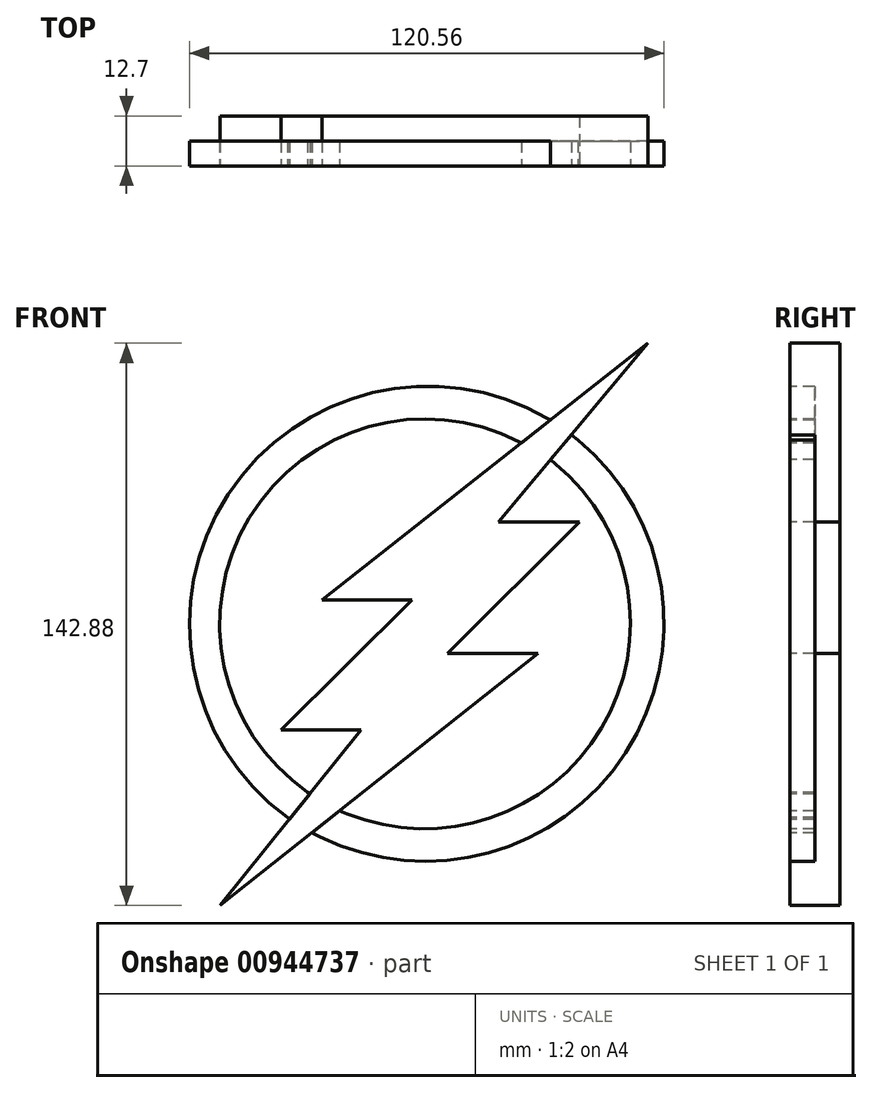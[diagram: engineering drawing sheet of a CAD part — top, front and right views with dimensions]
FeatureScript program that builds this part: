
annotation { "Feature Type Name" : "Feature", "Feature Type Description" : "" }
export const myFeature = defineFeature(function(context is Context, id is Id, definition is map)
    precondition{}
    {
        {
            var Q0;
            Q0=qCreatedBy(makeId("Front.planeOp"),FACE);
            var sketch = newSketch(context, id + "F0", { "sketchPlane" : qUnion([Q0])});
            skArc(sketch, "E0", {"start": v(8.9, 48.86) * mm, "mid": v(-59.71, 29.53) * mm, "end": v(-44.86, -40.17) * mm});
            skArc(sketch, "E1", {"start": v(-34.81, -45.6) * mm, "mid": v(29.76, -23.84) * mm, "end": v(18.12, 43.3) * mm});
            skArc(sketch, "E2", {"start": v(-41.74, -51.44) * mm, "mid": v(35.87, -30.16) * mm, "end": v(23.82, 49.4) * mm});
            skArc(sketch, "E3", {"start": v(16.08, 54.83) * mm, "mid": v(-65.07, 35.5) * mm, "end": v(-50.01, -46.55) * mm});
            skLineSegment(sketch, "E4", {"start": v(41.6, 73.97) * mm, "end": v(3.6, 28.5) * mm});
            skLineSegment(sketch, "E5", {"start": v(3.6, 28.5) * mm, "end": v(24.23, 28.5) * mm});
            skLineSegment(sketch, "E6", {"start": v(24.23, 28.5) * mm, "end": v(-9.3, -4.89) * mm});
            skLineSegment(sketch, "E7", {"start": v(-9.3, -4.89) * mm, "end": v(13.64, -4.89) * mm});
            skLineSegment(sketch, "E8", {"start": v(13.64, -4.89) * mm, "end": v(-65.08, -67.32) * mm});
            skLineSegment(sketch, "E9", {"start": v(-65.08, -67.32) * mm, "end": v(-67.09, -68.91) * mm});
            skLineSegment(sketch, "E10", {"start": v(-67.09, -68.91) * mm, "end": v(-31.27, -24.32) * mm});
            skLineSegment(sketch, "E11", {"start": v(-31.27, -24.32) * mm, "end": v(-51.63, -24.32) * mm});
            skLineSegment(sketch, "E12", {"start": v(-51.63, -24.32) * mm, "end": v(-18.38, 8.66) * mm});
            skLineSegment(sketch, "E13", {"start": v(-18.38, 8.66) * mm, "end": v(-41.18, 8.66) * mm});
            skLineSegment(sketch, "E14", {"start": v(-41.18, 8.66) * mm, "end": v(41.6, 73.97) * mm});
            skLineSegment(sketch, "E15", {"start": v(23.82, 49.4) * mm, "end": v(22.1, 50.64) * mm});
            skLineSegment(sketch, "E16", {"start": v(16.08, 54.83) * mm, "end": v(16.81, 54.41) * mm});
            skLineSegment(sketch, "E17", {"start": v(-50.01, -46.55) * mm, "end": v(-49.52, -47.05) * mm});
            skLineSegment(sketch, "E18", {"start": v(-41.74, -51.44) * mm, "end": v(-43.78, -50.43) * mm});
            skLineSegment(sketch, "E19", {"start": v(-41.18, 8.66) * mm, "end": v(-14.18, 19.27) * mm});
            skLineSegment(sketch, "E20", {"start": v(-14.18, 19.27) * mm, "end": v(3.6, 28.5) * mm});
            skLineSegment(sketch, "E21", {"start": v(-14.18, 19.27) * mm, "end": v(41.6, 73.97) * mm});
            skLineSegment(sketch, "E22", {"start": v(-14.18, 19.27) * mm, "end": v(2.38, 19.27) * mm});
            skLineSegment(sketch, "E23", {"start": v(2.38, 19.27) * mm, "end": v(24.23, 28.5) * mm});
            skLineSegment(sketch, "E24", {"start": v(2.38, 19.27) * mm, "end": v(-29.25, -14.25) * mm});
            skLineSegment(sketch, "E25", {"start": v(-29.25, -14.25) * mm, "end": v(-51.63, -24.32) * mm});
            skLineSegment(sketch, "E26", {"start": v(-29.25, -14.25) * mm, "end": v(-13.1, -14.25) * mm});
            skLineSegment(sketch, "E27", {"start": v(-13.1, -14.25) * mm, "end": v(13.64, -4.89) * mm});
            skLineSegment(sketch, "E28", {"start": v(-13.1, -14.25) * mm, "end": v(-67.09, -68.91) * mm});
            skLineSegment(sketch, "E29", {"start": v(-18.38, 8.66) * mm, "end": v(2.38, 19.27) * mm});
            skLineSegment(sketch, "E30", {"start": v(-31.27, -24.32) * mm, "end": v(-13.1, -14.25) * mm});
            skLineSegment(sketch, "E31", {"start": v(-29.25, -14.25) * mm, "end": v(-9.3, -4.89) * mm});
            skLineSegment(sketch, "E32", {"start": v(-34.81, -45.6) * mm, "end": v(-36.73, -44.83) * mm});
            skLineSegment(sketch, "E33", {"start": v(-44.27, -40.5) * mm, "end": v(-44.86, -40.17) * mm});
            skLineSegment(sketch, "E34", {"start": v(18.12, 43.3) * mm, "end": v(16.84, 44.35) * mm});
            skLineSegment(sketch, "E35", {"start": v(8.9, 48.86) * mm, "end": v(9.42, 48.58) * mm});
            skSolve(sketch);
        }
        {
            var Q0;
            Q0=makeQuery(id+"F0.imprint","IMPRINT",FACE,{"disambiguationData":[TD([[makeQuery(id+"F0.imprint","IMPRINT",EDGE,{"derivedFrom":sQuery(id+"F0.wireOp",EDGE,"E2")}),1.0]])]});
            var Q1;
            Q1=makeQuery(id+"F0.imprint","IMPRINT",FACE,{"disambiguationData":[TD([[makeQuery(id+"F0.imprint","IMPRINT",EDGE,{"derivedFrom":sQuery(id+"F0.wireOp",EDGE,"E3")}),1.0]])]});
            extrude(context, id + "F1", {"entities" : qUnion([Q0, Q1]), "oppositeDirection" : true, "depth" : 6.35 * mm, "offsetDistance" : 25.4 * mm});
        }
        {
            var Q0;
            {var subQ0=sQuery(id+"F0.wireOp",EDGE,"E19");Q0=makeQuery(id+"F0.imprint","IMPRINT",FACE,{"disambiguationData":[TD([[makeQuery(id+"F0.imprint","IMPRINT",EDGE,{"derivedFrom":subQ0}),1.0]])]});}
            var Q1;
            {var subQ0=sQuery(id+"F0.wireOp",EDGE,"E20");Q1=makeQuery(id+"F0.imprint","IMPRINT",FACE,{"disambiguationData":[TD([[makeQuery(id+"F0.imprint","IMPRINT",EDGE,{"derivedFrom":subQ0}),1.0]])]});}
            var Q2;
            Q2=makeQuery(id+"F0.imprint","IMPRINT",FACE,{"disambiguationData":[TD([[makeQuery(id+"F0.imprint","IMPRINT",EDGE,{"derivedFrom":sQuery(id+"F0.wireOp",EDGE,"E5")}),-1.0]])]});
            var Q3;
            Q3=makeQuery(id+"F0.imprint","IMPRINT",FACE,{"disambiguationData":[TD([[makeQuery(id+"F0.imprint","IMPRINT",EDGE,{"derivedFrom":sQuery(id+"F0.wireOp",EDGE,"E13")}),-1.0]])]});
            var Q4;
            Q4=makeQuery(id+"F0.imprint","IMPRINT",FACE,{"disambiguationData":[TD([[makeQuery(id+"F0.imprint","IMPRINT",EDGE,{"derivedFrom":sQuery(id+"F0.wireOp",EDGE,"E12")}),-1.0]])]});
            var Q5;
            Q5=makeQuery(id+"F0.imprint","IMPRINT",FACE,{"disambiguationData":[TD([[makeQuery(id+"F0.imprint","IMPRINT",EDGE,{"derivedFrom":sQuery(id+"F0.wireOp",EDGE,"E6")}),-1.0]])]});
            var Q6;
            Q6=makeQuery(id+"F0.imprint","IMPRINT",FACE,{"disambiguationData":[TD([[makeQuery(id+"F0.imprint","IMPRINT",EDGE,{"derivedFrom":sQuery(id+"F0.wireOp",EDGE,"E11")}),-1.0]])]});
            var Q7;
            {var subQ0=sQuery(id+"F0.wireOp",EDGE,"E28");Q7=makeQuery(id+"F0.imprint","IMPRINT",FACE,{"disambiguationData":[TD([[makeQuery(id+"F0.imprint","IMPRINT",EDGE,{"derivedFrom":subQ0}),-1.0]])]});}
            var Q8;
            {var subQ0=sQuery(id+"F0.wireOp",EDGE,"E9");Q8=makeQuery(id+"F0.imprint","IMPRINT",FACE,{"disambiguationData":[TD([[makeQuery(id+"F0.imprint","IMPRINT",EDGE,{"derivedFrom":subQ0}),-1.0]])]});}
            var Q9;
            Q9=makeQuery(id+"F0.imprint","IMPRINT",FACE,{"disambiguationData":[TD([[makeQuery(id+"F0.imprint","IMPRINT",EDGE,{"derivedFrom":sQuery(id+"F0.wireOp",EDGE,"E7")}),-1.0]])]});
            extrude(context, id + "F2", {"entities" : qUnion([Q0, Q1, Q2, Q3, Q4, Q5, Q6, Q7, Q8, Q9]), "oppositeDirection" : true, "depth" : 12.7 * mm, "offsetDistance" : 25.4 * mm});
        }
    });
